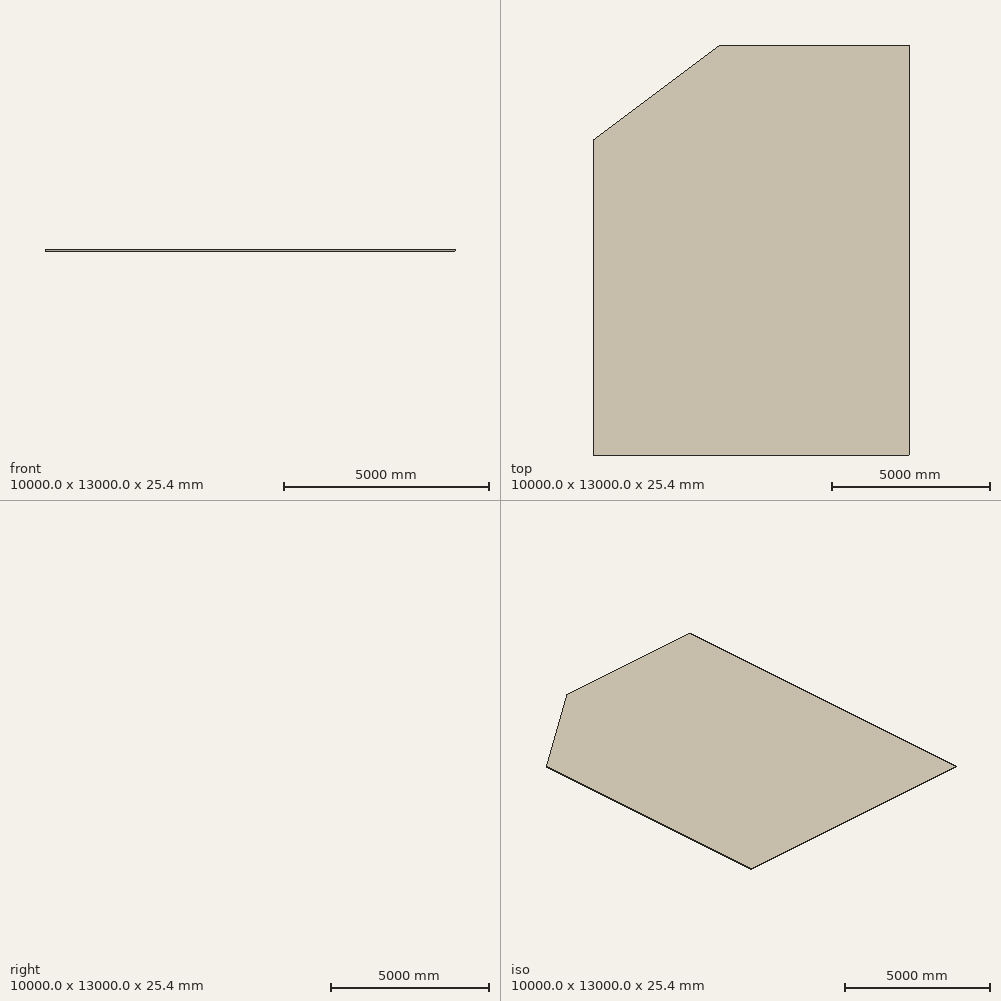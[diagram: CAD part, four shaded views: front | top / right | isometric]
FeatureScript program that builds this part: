
annotation { "Feature Type Name" : "Feature", "Feature Type Description" : "" }
export const myFeature = defineFeature(function(context is Context, id is Id, definition is map)
    precondition{}
    {
        {
            var Q0;
            Q0=qCreatedBy(makeId("Top.planeOp"),FACE);
            var sketch = newSketch(context, id + "F0", { "sketchPlane" : qUnion([Q0])});
            skLineSegment(sketch, "E0", {"start": v(6017.34, 5493.16) * mm, "end": v(6017.34, -7506.84) * mm});
            skLineSegment(sketch, "E1", {"start": v(6017.34, -7506.84) * mm, "end": v(-3982.66, -7506.84) * mm});
            skLineSegment(sketch, "E2", {"start": v(-3982.66, -7506.84) * mm, "end": v(-3982.66, 2493.16) * mm});
            skLineSegment(sketch, "E3", {"start": v(-3982.66, 2493.16) * mm, "end": v(17.34, 5493.16) * mm});
            skLineSegment(sketch, "E4", {"start": v(17.34, 5493.16) * mm, "end": v(6017.34, 5493.16) * mm});
            skSolve(sketch);
        }
        {
            var Q0;
            Q0=makeQuery(id+"F0.imprint","IMPRINT",FACE,{"disambiguationData":[TD([[makeQuery(id+"F0.imprint","IMPRINT",EDGE,{"derivedFrom":sQuery(id+"F0.wireOp",EDGE,"E0")}),-1.0]])]});
            extrude(context, id + "F1", {"entities" : qUnion([Q0]), "depth" : 25.4 * mm});
        }
    });
